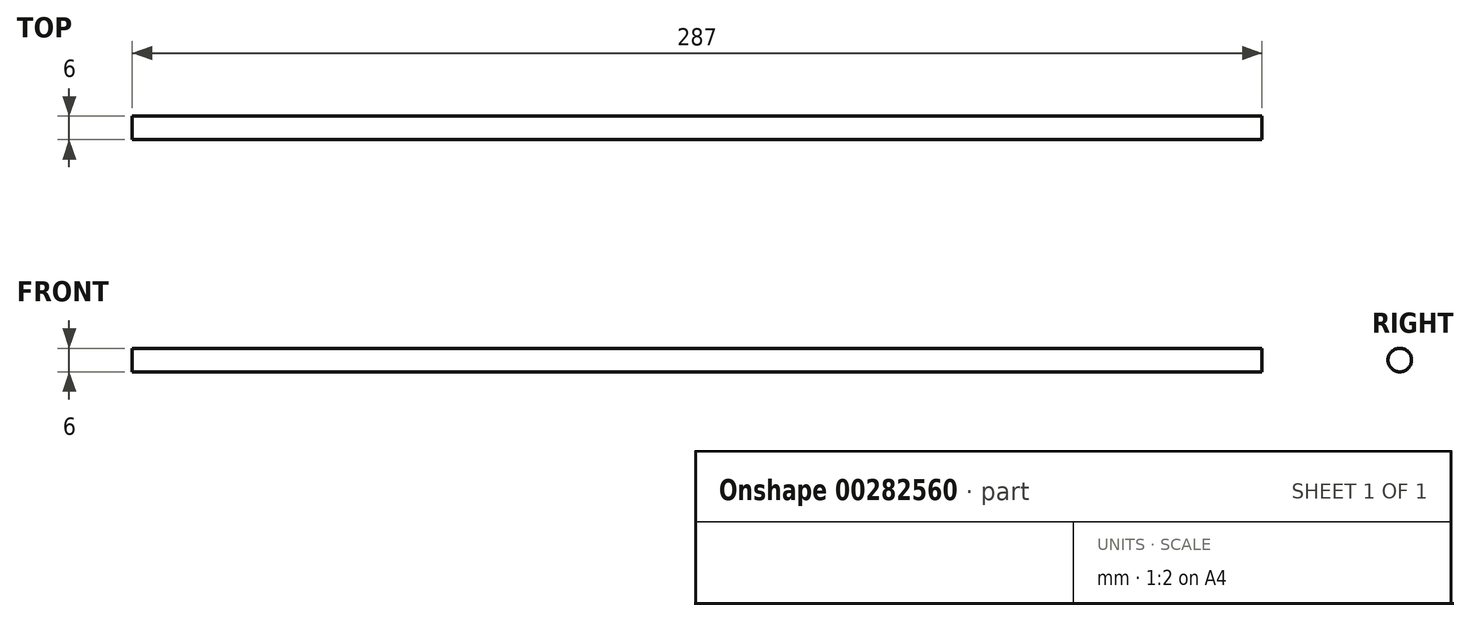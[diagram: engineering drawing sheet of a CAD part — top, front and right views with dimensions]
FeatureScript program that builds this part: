
annotation { "Feature Type Name" : "Feature", "Feature Type Description" : "" }
export const myFeature = defineFeature(function(context is Context, id is Id, definition is map)
    precondition{}
    {
        {
            var Q0;
            Q0=qCreatedBy(makeId("Right.planeOp"),FACE);
            var sketch = newSketch(context, id + "F0", { "sketchPlane" : qUnion([Q0])});
            skCircle(sketch, "E0", {"center": v(0, 0) * mm, "radius": 3 * mm});
            skSolve(sketch);
        }
        {
            var Q0;
            Q0=makeQuery(id+"F0.imprint","IMPRINT",FACE,{"disambiguationData":[TD([[makeQuery(id+"F0.imprint","IMPRINT",EDGE,{"derivedFrom":sQuery(id+"F0.wireOp",EDGE,"E0")}),1.0]])]});
            extrude(context, id + "F1", {"entities" : qUnion([Q0]), "depth" : 287 * mm});
        }
    });
